# Revit family: DYN
name_source: partatom
category: Lighting Fixtures
revit_build: Autodesk Revit 2013 (Build: 20120221_2030(x64)
units: mm (PartAtom-declared; Revit-internal decimal feet)

## types (2) — shared parameters
Assembly Code = D5020210
Connector Description = Lighting Connector
Default Elevation = 48 "
Description = NEMA 4X / C1D2 / C2D1 Industrial LED Emergency Light
Glass = Hubbell - Glass
Head Angle = 45.00°
Lamp = 2 lamp-heads with 3 high-power LEDs per head
Load Classification = Lighting
Manufacturer = Dual-Lite
Manufacturer Fax = 866-898-0131
Model = Dynamo DYN Series
Power Factor = 1
Product Documentation Link = http://cdn.dual-lite.com
Product Material = Finish - Hubbell - Gray
Product Page URL = http://www.dual-lite.com
URL = http://www.dual-lite.com
Voltage = 120 V
zz Angle1 = 45.00°

## per-type parameters (varying)
| type | Apparent Load | Photometry Web | Wattage Comments | Watts |
| DYN - 3W | 3 VA | Dynamo : 03 W | 3W Model | 3 W |
| DYN - 6W | 6 VA | Dynamo : 06 W | 6W Model | 6 W |

## geometry (parser evidence)
native form markers: Sweep x7
no freeform markers — native parametric forms only
